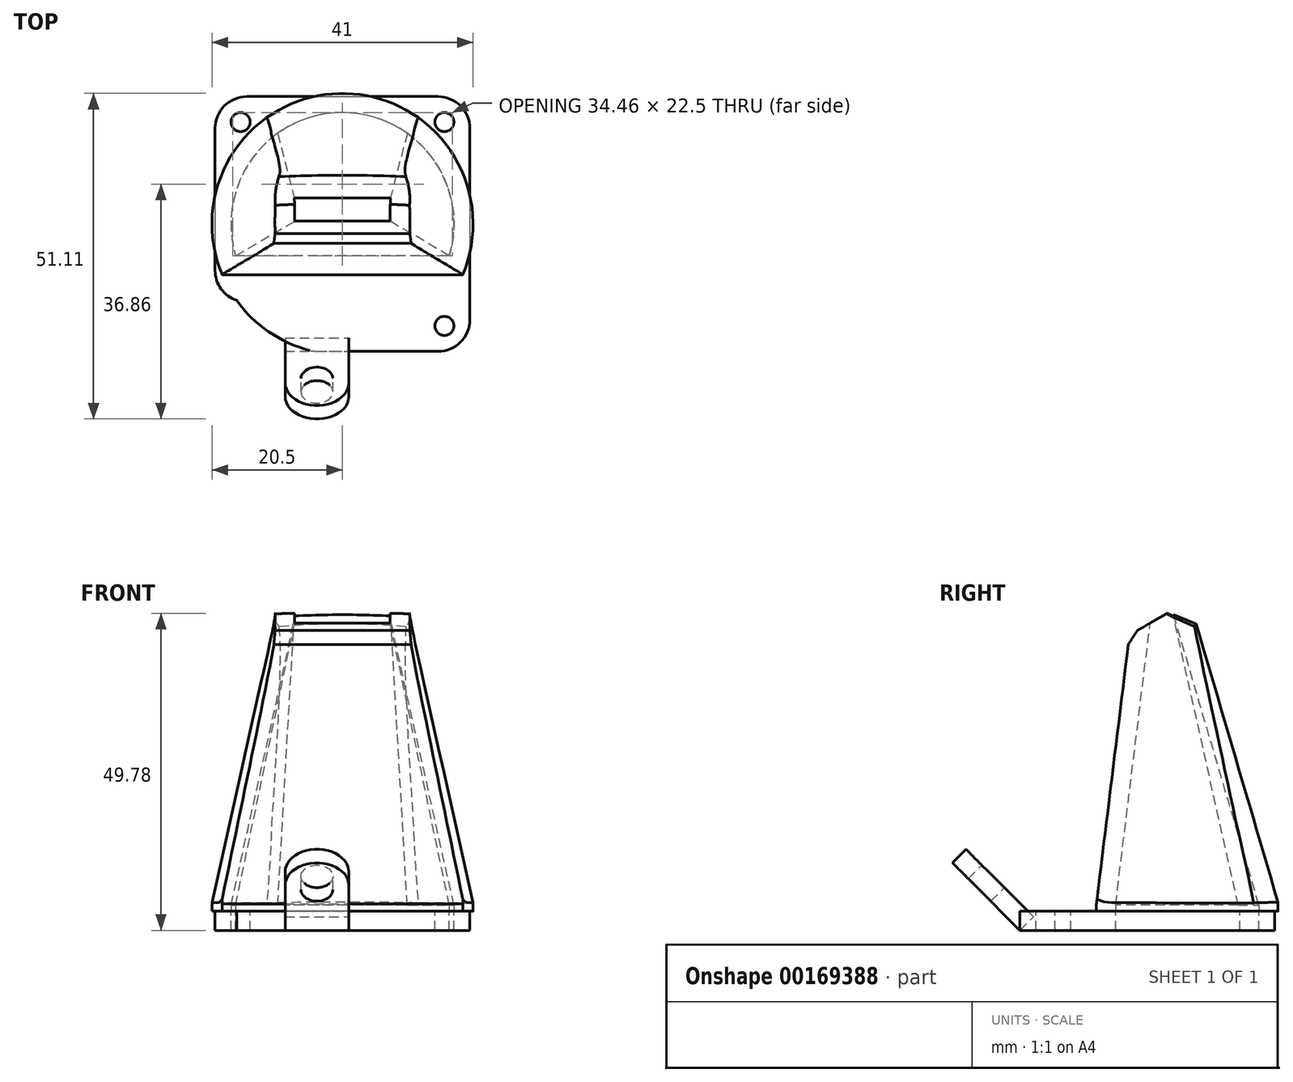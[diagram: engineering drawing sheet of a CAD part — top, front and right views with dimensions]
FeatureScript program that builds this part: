
annotation { "Feature Type Name" : "Feature", "Feature Type Description" : "" }
export const myFeature = defineFeature(function(context is Context, id is Id, definition is map)
    precondition{}
    {
        {
            var Q0;
            Q0=qCreatedBy(makeId("Top.planeOp"),FACE);
            var sketch = newSketch(context, id + "F0", { "sketchPlane" : qUnion([Q0])});
            skLineSegment(sketch, "E0.bottom", {"start": v(-20, 20) * mm, "end": v(20, 20) * mm});
            skLineSegment(sketch, "E0.top", {"start": v(-20, -20) * mm, "end": v(20, -20) * mm});
            skLineSegment(sketch, "E0.left", {"start": v(-20, 20) * mm, "end": v(-20, -20) * mm});
            skLineSegment(sketch, "E0.right", {"start": v(20, 20) * mm, "end": v(20, -20) * mm});
            skPoint(sketch, "E0.middle", {"position": v(0, 0) * mm});
            skPoint(sketch, "E1", {"position": v(-16, 16) * mm});
            skLineSegment(sketch, "E2", {"start": v(-20, 0) * mm, "end": v(20, 0) * mm, "construction": true});
            skLineSegment(sketch, "E3", {"start": v(0, 20) * mm, "end": v(0, -20) * mm, "construction": true});
            skPoint(sketch, "E4.MirrorP", {"position": v(16, 16) * mm});
            skPoint(sketch, "E5.MirrorP", {"position": v(-16, -16) * mm});
            skPoint(sketch, "E6.MirrorP", {"position": v(16, -16) * mm});
            skLineSegment(sketch, "E7.bottom", {"start": v(1, -20) * mm, "end": v(-9, -20) * mm});
            skLineSegment(sketch, "E7.top", {"start": v(1, -35) * mm, "end": v(-9, -35) * mm});
            skLineSegment(sketch, "E7.left", {"start": v(1, -20) * mm, "end": v(1, -35) * mm});
            skLineSegment(sketch, "E7.right", {"start": v(-9, -20) * mm, "end": v(-9, -35) * mm});
            skPoint(sketch, "E8", {"position": v(-4, -29) * mm});
            skCircle(sketch, "E9", {"center": v(0, 0) * mm, "radius": 17.5 * mm});
            skLineSegment(sketch, "E10", {"start": v(-20, -12) * mm, "end": v(-12.74, -12) * mm});
            skLineSegment(sketch, "E11.MirrorCS", {"start": v(20, -12) * mm, "end": v(12.74, -12) * mm});
            skLineSegment(sketch, "E12", {"start": v(16.77, -5) * mm, "end": v(-16.77, -5) * mm});
            skCircle(sketch, "E13.0", {"center": v(0, 0) * mm, "radius": 20.5 * mm});
            skLineSegment(sketch, "E14", {"start": v(-16.77, -5) * mm, "end": v(-19.88, -5) * mm});
            skLineSegment(sketch, "E15", {"start": v(16.77, -5) * mm, "end": v(19.88, -5) * mm});
            skLineSegment(sketch, "E16", {"start": v(0, 0) * mm, "end": v(-12.37, 12.37) * mm, "construction": true});
            skLineSegment(sketch, "E17", {"start": v(0, 0) * mm, "end": v(12.37, 12.37) * mm, "construction": true});
            skLineSegment(sketch, "E18", {"start": v(-12.37, 12.37) * mm, "end": v(-14.5, 14.5) * mm, "construction": true});
            skLineSegment(sketch, "E19", {"start": v(12.37, 12.37) * mm, "end": v(14.5, 14.5) * mm, "construction": true});
            skSolve(sketch);
        }
        {
            var Q0;
            {var subQ7=sQuery(id+"F0.wireOp",EDGE,"E7.bottom");Q0=makeQuery(id+"F0.imprint","IMPRINT",FACE,{"disambiguationData":[TD([[makeQuery(id+"F0.imprint","IMPRINT",EDGE,{"derivedFrom":subQ7}),-1.0]])]});}
            var Q1;
            {var subQ4=sQuery(id+"F0.wireOp",EDGE,"E0.bottom");Q1=makeQuery(id+"F0.imprint","IMPRINT",FACE,{"disambiguationData":[TD([[makeQuery(id+"F0.imprint","IMPRINT",EDGE,{"derivedFrom":subQ4}),-1.0]])]});}
            var Q2;
            {var subQ2=sQuery(id+"F0.wireOp",EDGE,"E12");Q2=makeQuery(id+"F0.imprint","IMPRINT",FACE,{"disambiguationData":[TD([[makeQuery(id+"F0.imprint","IMPRINT",EDGE,{"derivedFrom":subQ2}),1.0]])]});}
            var Q3;
            {var subQ0=sQuery(id+"F0.wireOp",EDGE,"E10");var subQ1=sQuery(id+"F0.wireOp",EDGE,"E9");var subQ2=makeQuery(id+"F0.imprint","INTERSECT",VERTEX,{"derivedFrom":[subQ1,subQ0]});Q3=makeQuery(id+"F0.imprint","IMPRINT",FACE,{"disambiguationData":[TD([[makeQuery(id+"F0.imprint","IMPRINT",EDGE,{"disambiguationData":[TD([[subQ2,1.0]])],"derivedFrom":subQ1}),-1.0]])]});}
            var Q4;
            {var subQ0=sQuery(id+"F0.wireOp",EDGE,"E10");var subQ1=sQuery(id+"F0.wireOp",EDGE,"E9");var subQ2=makeQuery(id+"F0.imprint","INTERSECT",VERTEX,{"derivedFrom":[subQ1,subQ0]});Q4=makeQuery(id+"F0.imprint","IMPRINT",FACE,{"disambiguationData":[TD([[makeQuery(id+"F0.imprint","IMPRINT",EDGE,{"disambiguationData":[TD([[subQ2,-1.0]])],"derivedFrom":subQ1}),-1.0]])]});}
            var Q5;
            {var subQ3=sQuery(id+"F0.wireOp",EDGE,"E14");Q5=makeQuery(id+"F0.imprint","IMPRINT",FACE,{"disambiguationData":[TD([[makeQuery(id+"F0.imprint","IMPRINT",EDGE,{"derivedFrom":subQ3}),-1.0]])]});}
            var Q6;
            {var subQ3=sQuery(id+"F0.wireOp",EDGE,"E15");Q6=makeQuery(id+"F0.imprint","IMPRINT",FACE,{"disambiguationData":[TD([[makeQuery(id+"F0.imprint","IMPRINT",EDGE,{"derivedFrom":subQ3}),-1.0]])]});}
            var Q7;
            {var subQ0=sQuery(id+"F0.wireOp",EDGE,"E18");Q7=makeQuery(id+"F0.imprint","IMPRINT",FACE,{"disambiguationData":[TD([[makeQuery(id+"F0.imprint","IMPRINT",EDGE,{"derivedFrom":subQ0}),-1.0]])]});}
            var Q8;
            {var subQ0=sQuery(id+"F0.wireOp",EDGE,"E15");Q8=makeQuery(id+"F0.imprint","IMPRINT",FACE,{"disambiguationData":[TD([[makeQuery(id+"F0.imprint","IMPRINT",EDGE,{"derivedFrom":subQ0}),1.0]])]});}
            var Q9;
            {var subQ0=sQuery(id+"F0.wireOp",EDGE,"E10");var subQ1=sQuery(id+"F0.wireOp",EDGE,"E0.left");var subQ2=makeQuery(id+"F0.imprint","INTERSECT",VERTEX,{"derivedFrom":[subQ1,subQ0]});Q9=makeQuery(id+"F0.imprint","IMPRINT",FACE,{"disambiguationData":[TD([[makeQuery(id+"F0.imprint","IMPRINT",EDGE,{"disambiguationData":[TD([[subQ2,1.0]])],"derivedFrom":subQ1}),1.0]])]});}
            var Q10;
            {var subQ0=sQuery(id+"F0.wireOp",EDGE,"E0.right");var subQ1=sQuery(id+"F0.wireOp",EDGE,"E0.top");var subQ2=makeQuery(id+"F0.imprint","INTERSECT",VERTEX,{"derivedFrom":[subQ1,subQ0]});Q10=makeQuery(id+"F0.imprint","IMPRINT",FACE,{"disambiguationData":[TD([[makeQuery(id+"F0.imprint","IMPRINT",EDGE,{"disambiguationData":[TD([[subQ2,1.0]])],"derivedFrom":subQ1}),1.0]])]});}
            var Q11;
            {var subQ0=sQuery(id+"F0.wireOp",EDGE,"E11.MirrorCS");var subQ1=sQuery(id+"F0.wireOp",EDGE,"E0.right");var subQ2=makeQuery(id+"F0.imprint","INTERSECT",VERTEX,{"derivedFrom":[subQ1,subQ0]});Q11=makeQuery(id+"F0.imprint","IMPRINT",FACE,{"disambiguationData":[TD([[makeQuery(id+"F0.imprint","IMPRINT",EDGE,{"disambiguationData":[TD([[subQ2,1.0]])],"derivedFrom":subQ1}),-1.0]])]});}
            extrude(context, id + "F1", {"entities" : qUnion([Q0, Q1, Q2, Q3, Q4, Q5, Q6, Q7, Q8, Q9, Q10, Q11]), "oppositeDirection" : true, "depth" : 3 * mm});
        }
        {
            var Q0;
            Q0=sQuery(id+"F0.wireOp",VERTEX,"E1");
            var Q1;
            Q1=sQuery(id+"F0.wireOp",VERTEX,"E4.MirrorP");
            var Q2;
            Q2=sQuery(id+"F0.wireOp",VERTEX,"E6.MirrorP");
            var Q3;
            Q3=sQuery(id+"F0.wireOp",VERTEX,"E5.MirrorP");
            var Q4;
            Q4=makeQuery(id+"F1.opExtrude","SWEPT_BODY",BODY,{"disambiguationData":[OSD([sQuery(id+"F0.wireOp",EDGE,"E0.bottom"),sQuery(id+"F0.wireOp",EDGE,"E0.top"),sQuery(id+"F0.wireOp",EDGE,"E0.left"),sQuery(id+"F0.wireOp",EDGE,"E0.right")])]});
            hole(context, id + "F2", {"style" : HoleStyle.SIMPLE, "endStyle" : HoleEndStyle.BLIND, "holeDiameter" : 3 * mm, "holeDepth" : 10 * mm, "locations" : qUnion([Q0, Q1, Q2, Q3]), "scope" : qUnion([Q4])});
        }
        {
            var Q0;
            Q0=makeQuery(id+"F1.opExtrude","SWEPT_EDGE",EDGE,{"disambiguationData":[OSD([sQuery(id+"F0.wireOp",EDGE,"E0.bottom"),sQuery(id+"F0.wireOp",EDGE,"E0.left")])]});
            var Q1;
            Q1=makeQuery(id+"F1.opExtrude","SWEPT_EDGE",EDGE,{"disambiguationData":[OSD([sQuery(id+"F0.wireOp",EDGE,"E0.top"),sQuery(id+"F0.wireOp",EDGE,"E0.left")])]});
            var Q2;
            Q2=makeQuery(id+"F1.opExtrude","SWEPT_EDGE",EDGE,{"disambiguationData":[OSD([sQuery(id+"F0.wireOp",EDGE,"E0.top"),sQuery(id+"F0.wireOp",EDGE,"E0.right")])]});
            var Q3;
            Q3=makeQuery(id+"F1.opExtrude","SWEPT_EDGE",EDGE,{"disambiguationData":[OSD([sQuery(id+"F0.wireOp",EDGE,"E0.bottom"),sQuery(id+"F0.wireOp",EDGE,"E0.right")])]});
            var Q4;
            Q4=makeQuery(id+"F1.opExtrude","SWEPT_EDGE",EDGE,{"disambiguationData":[OSD([sQuery(id+"F0.wireOp",EDGE,"E7.top"),sQuery(id+"F0.wireOp",EDGE,"E7.right")])]});
            var Q5;
            Q5=makeQuery(id+"F1.opExtrude","SWEPT_EDGE",EDGE,{"disambiguationData":[OSD([sQuery(id+"F0.wireOp",EDGE,"E7.top"),sQuery(id+"F0.wireOp",EDGE,"E7.left")])]});
            fillet(context, id + "F3", {"entities" : qUnion([Q0, Q1, Q2, Q3, Q4, Q5]), "radius" : 5 * mm, "tangentPropagation" : true, "allowEdgeOverflow" : false});
        }
        {
            var Q0;
            {var subQ2=sQuery(id+"F0.wireOp",EDGE,"E7.top");Q0=makeQuery(id+"F0.imprint","IMPRINT",FACE,{"disambiguationData":[TD([[makeQuery(id+"F0.imprint","IMPRINT",EDGE,{"derivedFrom":subQ2}),-1.0]])]});}
            var Q1;
            {var subQ0=sQuery(id+"F0.wireOp",EDGE,"E7.left");var subQ3=sQuery(id+"F0.wireOp",EDGE,"E13.0");var subQ5=makeQuery(id+"F0.imprint","INTERSECT",VERTEX,{"derivedFrom":[subQ0,subQ3]});Q1=makeQuery(id+"F0.imprint","IMPRINT",FACE,{"disambiguationData":[TD([[makeQuery(id+"F0.imprint","IMPRINT",EDGE,{"disambiguationData":[TD([[subQ5,1.0]])],"derivedFrom":subQ3}),1.0]])]});}
            extrude(context, id + "F4", {"entities" : qUnion([Q0, Q1]), "oppositeDirection" : true, "depth" : 3 * mm});
        }
        {
            var Q0;
            Q0=makeQuery(id+"F4.opExtrude","SWEPT_EDGE",EDGE,{"disambiguationData":[OSD([sQuery(id+"F0.wireOp",EDGE,"E7.top"),sQuery(id+"F0.wireOp",EDGE,"E7.right")])]});
            var Q1;
            Q1=makeQuery(id+"F4.opExtrude","SWEPT_EDGE",EDGE,{"disambiguationData":[OSD([sQuery(id+"F0.wireOp",EDGE,"E7.top"),sQuery(id+"F0.wireOp",EDGE,"E7.left")])]});
            fillet(context, id + "F5", {"entities" : qUnion([Q0, Q1]), "radius" : 5 * mm, "tangentPropagation" : true, "allowEdgeOverflow" : false});
        }
        {
            var Q0;
            Q0=sQuery(id+"F0.wireOp",VERTEX,"E8");
            var Q1;
            Q1=makeQuery(id+"F4.opExtrude","SWEPT_BODY",BODY,{"disambiguationData":[OSD([sQuery(id+"F0.wireOp",EDGE,"E7.bottom"),sQuery(id+"F0.wireOp",EDGE,"E7.top"),sQuery(id+"F0.wireOp",EDGE,"E7.left"),sQuery(id+"F0.wireOp",EDGE,"E7.right")])]});
            hole(context, id + "F6", {"style" : HoleStyle.SIMPLE, "endStyle" : HoleEndStyle.BLIND, "holeDiameter" : 5 * mm, "holeDepth" : 10 * mm, "locations" : qUnion([Q0]), "scope" : qUnion([Q1])});
        }
        {
            var Q0;
            Q0=makeQuery(id+"F4.opExtrude","SWEPT_BODY",BODY,{"disambiguationData":[OSD([sQuery(id+"F0.wireOp",EDGE,"E7.bottom"),sQuery(id+"F0.wireOp",EDGE,"E7.top"),sQuery(id+"F0.wireOp",EDGE,"E7.left"),sQuery(id+"F0.wireOp",EDGE,"E7.right")])]});
            var Q1;
            Q1=makeQuery(id+"F1.opExtrude","CAP_EDGE",EDGE,{"disambiguationData":[OSD([sQuery(id+"F0.wireOp",EDGE,"E0.top"),sQuery(id+"F0.wireOp",EDGE,"E7.bottom")])],"isStart":false});
            transform(context, id + "F7", {"entities" : qUnion([Q0]), "transformType" : TransformType.ROTATION, "transformAxis" : qUnion([Q1]), "angle" : 45 * degree, "oppositeDirection" : true, "makeCopy" : false});
        }
        {
            var Q0;
            Q0=qCreatedBy(makeId("Top.planeOp"),FACE);
            cPlane(context, id + "F8", {"entities" : qUnion([Q0]), "cplaneType" : CPlaneType.OFFSET, "offset" : 45 * mm, "width" : 150 * mm, "height" : 150 * mm});
        }
        {
            var Q0;
            Q0=qCreatedBy(id+"F8.planeOp",FACE);
            var sketch = newSketch(context, id + "F9", { "sketchPlane" : qUnion([Q0])});
            skLineSegment(sketch, "E20", {"start": v(-74.78, 0) * mm, "end": v(74.46, 0) * mm});
            skSolve(sketch);
        }
        {
            var Q0;
            Q0=sQuery(id+"F9.wireOp",EDGE,"E20");
            cPlane(context, id + "F10", {"entities" : qUnion([Q0]), "cplaneType" : CPlaneType.LINE_ANGLE, "offset" : 25 * mm, "angle" : 120 * degree, "width" : 150 * mm, "height" : 150 * mm});
        }
        {
            var Q0;
            Q0=qCreatedBy(id+"F10.planeOp",FACE);
            var sketch = newSketch(context, id + "F11", { "sketchPlane" : qUnion([Q0])});
            skLineSegment(sketch, "E21.bottom", {"start": v(-7.5, 27) * mm, "end": v(7.5, 27) * mm});
            skLineSegment(sketch, "E21.top", {"start": v(-7.5, 23) * mm, "end": v(7.5, 23) * mm});
            skLineSegment(sketch, "E21.left", {"start": v(-7.5, 27) * mm, "end": v(-7.5, 23) * mm});
            skLineSegment(sketch, "E21.right", {"start": v(7.5, 27) * mm, "end": v(7.5, 23) * mm});
            skPoint(sketch, "E21.middle", {"position": v(0, 25) * mm});
            skSolve(sketch);
        }
        {
            var Q0;
            {var subQ0=sQuery(id+"F0.wireOp",EDGE,"E12");Q0=makeQuery(id+"F0.imprint","IMPRINT",FACE,{"disambiguationData":[TD([[makeQuery(id+"F0.imprint","IMPRINT",EDGE,{"derivedFrom":subQ0}),-1.0]])]});}
            extrude(context, id + "F12", {"entities" : qUnion([Q0]), "depth" : 1 * mm});
        }
        {
            var Q1;
            Q1=makeQuery(id+"F12.opExtrude","CAP_FACE",FACE,{"disambiguationData":[OSD([sQuery(id+"F0.wireOp",EDGE,"E12"),sQuery(id+"F0.wireOp",EDGE,"E13.0"),sQuery(id+"F0.wireOp",EDGE,"E14"),sQuery(id+"F0.wireOp",EDGE,"E15")])],"isStart":false});
            var Q2;
            Q2=makeQuery(id+"F11.imprint","IMPRINT",FACE,{"disambiguationData":[TD([[makeQuery(id+"F11.imprint","IMPRINT",EDGE,{"derivedFrom":sQuery(id+"F11.wireOp",EDGE,"E21.bottom")}),-1.0]])]});
            loft(context, id + "F13", {"operationType" : NewBodyOperationType.ADD, "sheetProfilesArray" : [{ "sheetProfileEntities" : qUnion([Q1]) }, { "sheetProfileEntities" : qUnion([Q2]) }]});
        }
        {
            var Q0;
            Q0=makeQuery(id+"F12.opExtrude","CAP_FACE",FACE,{"disambiguationData":[OSD([sQuery(id+"F0.wireOp",EDGE,"E9"),sQuery(id+"F0.wireOp",EDGE,"E12")])],"isStart":true});
            var Q1;
            Q1=makeQuery(id+"F13.opLoft","CAP_FACE",FACE,{"disambiguationData":[OSD([makeQuery(id+"F11.imprint","IMPRINT",FACE,{"disambiguationData":[TD([[makeQuery(id+"F11.imprint","IMPRINT",EDGE,{"derivedFrom":sQuery(id+"F11.wireOp",EDGE,"E21.bottom")}),-1.0]])]})])],"isStart":true});
            shell(context, id + "F14", {"entities" : qUnion([Q0, Q1]), "thickness" : 3 * mm, "oppositeDirection" : true});
        }
        {
            var Q0;
            Q0=makeQuery(id+"F13.opLoft","MID_CAP_EDGE",EDGE,{"disambiguationData":[OSD([sQuery(id+"F11.wireOp",EDGE,"E21.bottom"),sQuery(id+"F11.wireOp",EDGE,"E21.left"),sQuery(id+"F11.wireOp",EDGE,"E21.right")])],"capPos":1.0});
            chamfer(context, id + "F15", {"entities" : qUnion([Q0]), "width" : 3 * mm, "tangentPropagation" : true});
        }
        {
            var Q0;
            Q0=makeQuery(id+"F13.opLoft","CAP_FACE",FACE,{"disambiguationData":[OSD([makeQuery(id+"F11.imprint","IMPRINT",FACE,{"disambiguationData":[TD([[makeQuery(id+"F11.imprint","IMPRINT",EDGE,{"derivedFrom":sQuery(id+"F11.wireOp",EDGE,"E21.bottom")}),-1.0]])]})])],"isStart":true});
            var sketch = newSketch(context, id + "F16", { "sketchPlane" : qUnion([Q0])});
            skLineSegment(sketch, "E22.bottom", {"start": v(-15.3, 33.3) * mm, "end": v(15.62, 33.3) * mm});
            skLineSegment(sketch, "E22.top", {"start": v(-15.3, 16.87) * mm, "end": v(15.62, 16.87) * mm});
            skLineSegment(sketch, "E22.left", {"start": v(-15.3, 33.3) * mm, "end": v(-15.3, 16.87) * mm});
            skLineSegment(sketch, "E22.right", {"start": v(15.62, 33.3) * mm, "end": v(15.62, 16.87) * mm});
            skSolve(sketch);
        }
        {
            var Q0;
            Q0=makeQuery(id+"F16.imprint","IMPRINT",FACE,{"disambiguationData":[TD([[makeQuery(id+"F16.imprint","IMPRINT",EDGE,{"derivedFrom":sQuery(id+"F16.wireOp",EDGE,"E22.bottom")}),-1.0]])]});
            var Q1;
            {var subQ0=sQuery(id+"F11.wireOp",EDGE,"E21.right");var subQ1=sQuery(id+"F11.wireOp",EDGE,"E21.top");var subQ3=sQuery(id+"F11.wireOp",EDGE,"E21.left");Q1=makeQuery(id+"F16.imprint","IMPRINT",FACE,{"disambiguationData":[TD([[makeQuery(id+"F16.imprint","IMPRINT",EDGE,{"derivedFrom":makeQuery(id+"F13.opLoft","MID_CAP_EDGE",EDGE,{"disambiguationData":[OSD([subQ1,subQ3,subQ0])],"capPos":1.0})}),1.0]])]});}
            var Q2;
            {var subQ0=sQuery(id+"F11.wireOp",EDGE,"E21.right");var subQ1=sQuery(id+"F11.wireOp",EDGE,"E21.left");var subQ2=sQuery(id+"F11.wireOp",EDGE,"E21.bottom");Q2=makeQuery(id+"F16.imprint","IMPRINT",FACE,{"disambiguationData":[TD([[makeQuery(id+"F16.imprint","IMPRINT",EDGE,{"derivedFrom":makeQuery(id+"F14.opShell","OFFSET_EDGE",EDGE,{"disambiguationData":[OSD([subQ2,subQ1,subQ0])]})}),1.0]])]});}
            extrude(context, id + "F17", {"entities" : qUnion([Q0, Q1, Q2]), "depth" : 5 * mm});
        }
        {
            var Q0;
            {var subQ0=sQuery(id+"F11.wireOp",EDGE,"E21.bottom");var subQ1=sQuery(id+"F11.wireOp",EDGE,"E21.left");var subQ2=sQuery(id+"F11.wireOp",EDGE,"E21.top");var subQ3=sQuery(id+"F11.wireOp",EDGE,"E21.right");Q0=makeQuery(id+"F17.opExtrude","SWEPT_BODY",BODY,{"disambiguationData":[OSD([subQ0,subQ2,subQ1,subQ3,makeQuery(id+"F11.imprint","IMPRINT",FACE,{"disambiguationData":[TD([[makeQuery(id+"F11.imprint","IMPRINT",EDGE,{"derivedFrom":subQ0}),-1.0]])]}),sQuery(id+"F16.wireOp",EDGE,"E22.bottom"),sQuery(id+"F16.wireOp",EDGE,"E22.top"),sQuery(id+"F16.wireOp",EDGE,"E22.left"),sQuery(id+"F16.wireOp",EDGE,"E22.right")])]});}
            var Q1;
            Q1=makeQuery(id+"F13.opLoft","MID_CAP_EDGE",EDGE,{"disambiguationData":[OSD([sQuery(id+"F11.wireOp",EDGE,"E21.top"),sQuery(id+"F11.wireOp",EDGE,"E21.left"),sQuery(id+"F11.wireOp",EDGE,"E21.right")])],"capPos":1.0});
            transform(context, id + "F18", {"entities" : qUnion([Q0]), "transformType" : TransformType.ROTATION, "transformAxis" : qUnion([Q1]), "angle" : 28 * degree, "makeCopy" : false});
        }
        {
            var Q0;
            Q0=makeQuery(id+"F17.opExtrude","SWEPT_BODY",BODY,{"disambiguationData":[OSD([sQuery(id+"F11.wireOp",EDGE,"E21.bottom"),sQuery(id+"F11.wireOp",EDGE,"E21.top"),sQuery(id+"F11.wireOp",EDGE,"E21.left"),sQuery(id+"F11.wireOp",EDGE,"E21.right"),sQuery(id+"F16.wireOp",EDGE,"E22.bottom"),sQuery(id+"F16.wireOp",EDGE,"E22.top"),sQuery(id+"F16.wireOp",EDGE,"E22.left"),sQuery(id+"F16.wireOp",EDGE,"E22.right")])]});
            var Q1;
            Q1=makeQuery(id+"F1.opExtrude","SWEPT_BODY",BODY,{"disambiguationData":[OSD([sQuery(id+"F0.wireOp",EDGE,"E0.bottom"),sQuery(id+"F0.wireOp",EDGE,"E0.top"),sQuery(id+"F0.wireOp",EDGE,"E0.left"),sQuery(id+"F0.wireOp",EDGE,"E0.right"),sQuery(id+"F0.wireOp",EDGE,"E7.bottom"),sQuery(id+"F0.wireOp",EDGE,"E9"),sQuery(id+"F0.wireOp",EDGE,"E12")])]});
            booleanBodies(context, id + "F19", {"operationType" : BooleanOperationType.SUBTRACTION, "tools" : qUnion([Q0]), "targets" : qUnion([Q1])});
        }
        {
            var Q0;
            Q0=makeQuery(id+"F13.opLoft","MID_CAP_EDGE",EDGE,{"disambiguationData":[OSD([sQuery(id+"F11.wireOp",EDGE,"E21.top"),sQuery(id+"F11.wireOp",EDGE,"E21.left"),sQuery(id+"F11.wireOp",EDGE,"E21.right")])],"capPos":1.0});
            var Q1;
            Q1=makeQuery(id+"F19.opBoolean","INTERSECT",EDGE,{"derivedFrom":[makeQuery(id+"F13.opLoft","SWEPT_FACE",FACE,{"disambiguationData":[OSD([sQuery(id+"F0.wireOp",EDGE,"E9"),sQuery(id+"F11.wireOp",EDGE,"E21.bottom"),sQuery(id+"F11.wireOp",EDGE,"E21.top"),sQuery(id+"F11.wireOp",EDGE,"E21.left"),sQuery(id+"F11.wireOp",EDGE,"E21.right")])]}),makeQuery(id+"F17.opExtrude","CAP_FACE",FACE,{"disambiguationData":[OSD([sQuery(id+"F16.wireOp",EDGE,"E22.bottom"),sQuery(id+"F16.wireOp",EDGE,"E22.top"),sQuery(id+"F16.wireOp",EDGE,"E22.left"),sQuery(id+"F16.wireOp",EDGE,"E22.right")])],"isStart":true})]});
            chamfer(context, id + "F20", {"entities" : qUnion([Q0, Q1]), "width" : 3 * mm, "tangentPropagation" : true});
        }
    });
